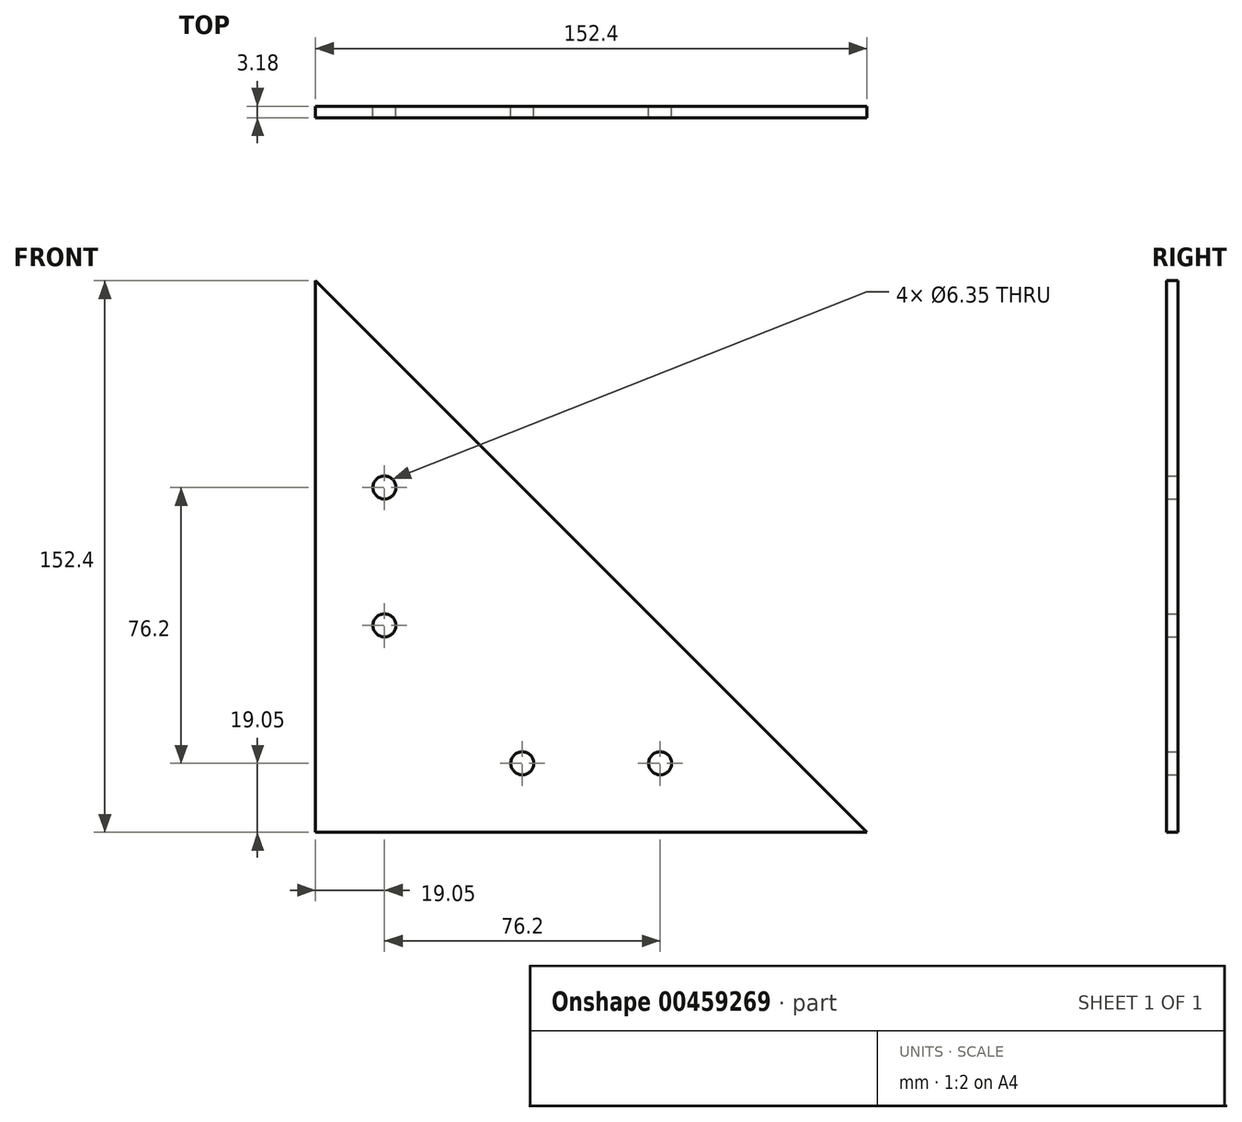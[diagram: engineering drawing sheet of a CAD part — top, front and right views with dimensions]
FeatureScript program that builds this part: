
annotation { "Feature Type Name" : "Feature", "Feature Type Description" : "" }
export const myFeature = defineFeature(function(context is Context, id is Id, definition is map)
    precondition{}
    {
        {
            var Q0;
            Q0=qCreatedBy(makeId("Front.planeOp"),FACE);
            var sketch = newSketch(context, id + "F0", { "sketchPlane" : qUnion([Q0])});
            skLineSegment(sketch, "E0", {"start": v(0, 0) * mm, "end": v(0, 152.4) * mm});
            skLineSegment(sketch, "E1", {"start": v(0, 152.4) * mm, "end": v(152.4, 0) * mm});
            skLineSegment(sketch, "E2", {"start": v(152.4, 0) * mm, "end": v(0, 0) * mm});
            skSolve(sketch);
        }
        {
            var Q0;
            Q0=makeQuery(id+"F0.imprint","IMPRINT",FACE,{"disambiguationData":[TD([[makeQuery(id+"F0.imprint","IMPRINT",EDGE,{"derivedFrom":sQuery(id+"F0.wireOp",EDGE,"E0")}),-1.0]])]});
            extrude(context, id + "F1", {"entities" : qUnion([Q0]), "depth" : 3.17 * mm});
        }
        {
            var Q0;
            Q0=qCreatedBy(makeId("Front.planeOp"),FACE);
            var sketch = newSketch(context, id + "F2", { "sketchPlane" : qUnion([Q0])});
            skLineSegment(sketch, "E3", {"start": v(0, 0) * mm, "end": v(19.05, 0) * mm, "construction": true});
            skLineSegment(sketch, "E4", {"start": v(0, 0) * mm, "end": v(0, 19.05) * mm, "construction": true});
            skLineSegment(sketch, "E5", {"start": v(0, 19.05) * mm, "end": v(140.45, 19.05) * mm, "construction": true});
            skLineSegment(sketch, "E6", {"start": v(19.05, 0) * mm, "end": v(19.05, 19.05) * mm, "construction": true});
            skLineSegment(sketch, "E7", {"start": v(19.05, 19.05) * mm, "end": v(19.05, 144.99) * mm, "construction": true});
            skCircle(sketch, "E8", {"center": v(19.05, 57.15) * mm, "radius": 3.18 * mm});
            skCircle(sketch, "E9", {"center": v(19.05, 95.25) * mm, "radius": 3.18 * mm});
            skCircle(sketch, "E10", {"center": v(57.15, 19.05) * mm, "radius": 3.18 * mm});
            skCircle(sketch, "E11", {"center": v(95.25, 19.05) * mm, "radius": 3.18 * mm});
            skSolve(sketch);
        }
        {
            var Q0;
            Q0 = qSketchRegion(id + "F2", true);
            extrude(context, id + "F3", {"entities" : qUnion([Q0]), "operationType" : NewBodyOperationType.REMOVE, "depth" : 76.2 * mm, "symmetric" : true});
        }
    });
